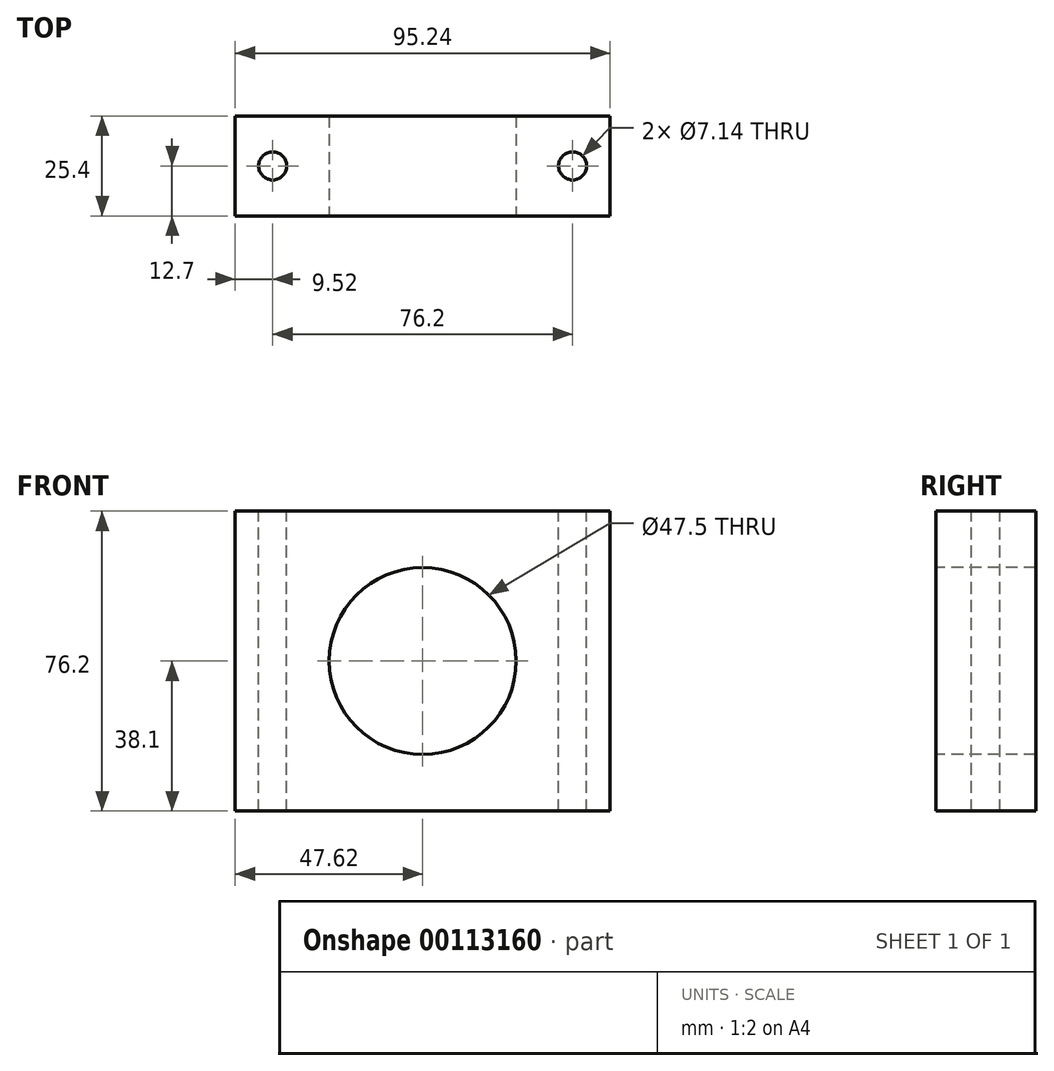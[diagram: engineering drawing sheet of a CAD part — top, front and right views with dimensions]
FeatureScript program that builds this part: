
annotation { "Feature Type Name" : "Feature", "Feature Type Description" : "" }
export const myFeature = defineFeature(function(context is Context, id is Id, definition is map)
    precondition{}
    {
        {
            var Q0;
            Q0=qCreatedBy(makeId("Front.planeOp"),FACE);
            var sketch = newSketch(context, id + "F0", { "sketchPlane" : qUnion([Q0])});
            skLineSegment(sketch, "E0.bottom", {"start": v(47.63, -38.1) * mm, "end": v(-47.62, -38.1) * mm});
            skLineSegment(sketch, "E0.top", {"start": v(47.62, 38.1) * mm, "end": v(-47.63, 38.1) * mm});
            skLineSegment(sketch, "E0.left", {"start": v(47.63, -38.1) * mm, "end": v(47.62, 38.1) * mm});
            skLineSegment(sketch, "E0.right", {"start": v(-47.62, -38.1) * mm, "end": v(-47.63, 38.1) * mm});
            skPoint(sketch, "E0.middle", {"position": v(0, 0) * mm});
            skCircle(sketch, "E1", {"center": v(0, 0) * mm, "radius": 23.75 * mm});
            skSolve(sketch);
        }
        {
            var Q0;
            Q0 = qSketchRegion(id + "F0", true);
            extrude(context, id + "F1", {"entities" : qUnion([Q0]), "oppositeDirection" : true, "depth" : 25.4 * mm});
        }
        {
            var Q0;
            Q0=qCreatedBy(makeId("Right.planeOp"),FACE);
            var sketch = newSketch(context, id + "F2", { "sketchPlane" : qUnion([Q0])});
            skSolve(sketch);
        }
        {
            var Q0;
            Q0=qCreatedBy(makeId("Top.planeOp"),FACE);
            var sketch = newSketch(context, id + "F3", { "sketchPlane" : qUnion([Q0])});
            skCircle(sketch, "E2", {"center": v(-38.1, 12.7) * mm, "radius": 3.57 * mm});
            skCircle(sketch, "E3.MirrorC", {"center": v(38.1, 12.7) * mm, "radius": 3.57 * mm});
            skSolve(sketch);
        }
        {
            var Q0;
            Q0 = qSketchRegion(id + "F3", true);
            extrude(context, id + "F4", {"entities" : qUnion([Q0]), "operationType" : NewBodyOperationType.REMOVE, "oppositeDirection" : true, "depth" : 38.1 * mm, "hasSecondDirection" : true, "secondDirectionOppositeDirection" : false, "secondDirectionDepth" : 38.1 * mm});
        }
    });
